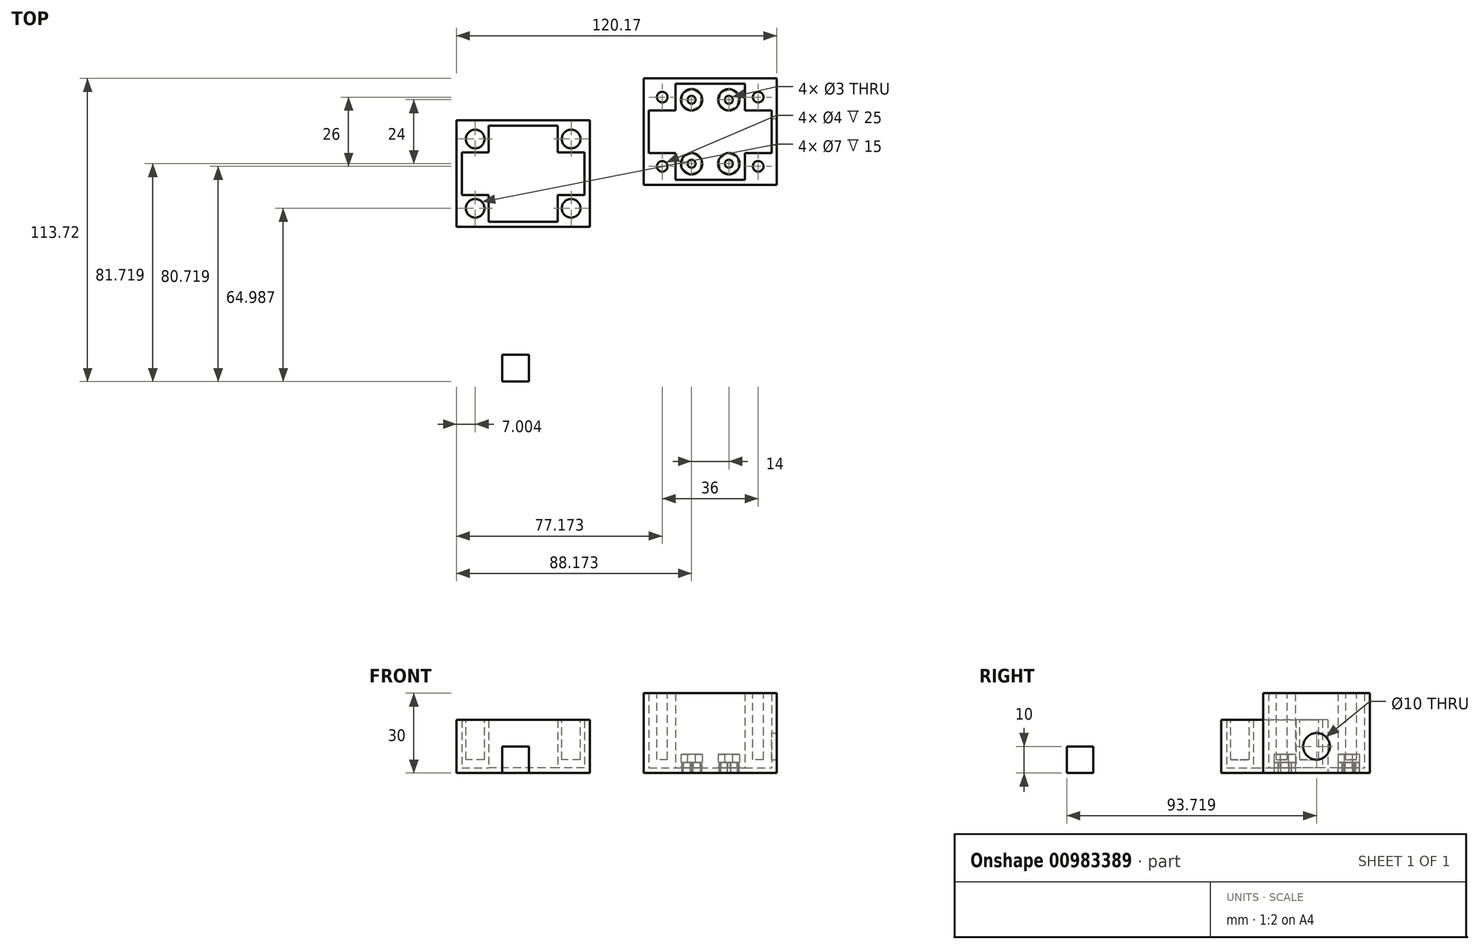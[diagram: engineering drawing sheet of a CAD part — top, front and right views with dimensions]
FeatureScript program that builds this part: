
annotation { "Feature Type Name" : "Feature", "Feature Type Description" : "" }
export const myFeature = defineFeature(function(context is Context, id is Id, definition is map)
    precondition{}
    {
        {
            var Q0;
            Q0=qCreatedBy(makeId("Top.planeOp"),FACE);
            var sketch = newSketch(context, id + "F0", { "sketchPlane" : qUnion([Q0])});
            skLineSegment(sketch, "E0.bottom", {"start": v(-58.4, 57.82) * mm, "end": v(-8.4, 57.82) * mm});
            skLineSegment(sketch, "E0.top", {"start": v(-58.4, 17.82) * mm, "end": v(-8.4, 17.82) * mm});
            skLineSegment(sketch, "E0.left", {"start": v(-58.4, 57.82) * mm, "end": v(-58.4, 17.82) * mm});
            skLineSegment(sketch, "E0.right", {"start": v(-8.4, 57.82) * mm, "end": v(-8.4, 17.82) * mm});
            skSolve(sketch);
        }
        {
            var Q0;
            Q0=makeQuery(id+"F0.imprint","IMPRINT",FACE,{"disambiguationData":[TD([[makeQuery(id+"F0.imprint","IMPRINT",EDGE,{"derivedFrom":sQuery(id+"F0.wireOp",EDGE,"E0.bottom")}),-1.0]])]});
            extrude(context, id + "F1", {"entities" : qUnion([Q0]), "depth" : 20 * mm, "offsetDistance" : 25 * mm});
        }
        {
            var Q0;
            Q0=makeQuery(id+"F1.opExtrude","CAP_FACE",FACE,{"disambiguationData":[OSD([sQuery(id+"F0.wireOp",EDGE,"E0.bottom"),sQuery(id+"F0.wireOp",EDGE,"E0.top"),sQuery(id+"F0.wireOp",EDGE,"E0.left"),sQuery(id+"F0.wireOp",EDGE,"E0.right")])],"isStart":false});
            var sketch = newSketch(context, id + "F2", { "sketchPlane" : qUnion([Q0])});
            skLineSegment(sketch, "E1.bottom", {"start": v(-10.4, 19.82) * mm, "end": v(-56.4, 19.82) * mm});
            skLineSegment(sketch, "E1.top", {"start": v(-10.4, 55.82) * mm, "end": v(-56.4, 55.82) * mm});
            skLineSegment(sketch, "E1.left", {"start": v(-10.4, 19.82) * mm, "end": v(-10.4, 55.82) * mm});
            skLineSegment(sketch, "E1.right", {"start": v(-56.4, 19.82) * mm, "end": v(-56.4, 55.82) * mm});
            skPoint(sketch, "E1.middle", {"position": v(-33.4, 37.82) * mm});
            skPoint(sketch, "E1.middle.positionSnap0", {"position": v(-58.4, 37.82) * mm});
            skPoint(sketch, "E1.middle.positionSnap1", {"position": v(-33.4, 57.82) * mm});
            skPoint(sketch, "E1.centerSnap0", {"position": v(-58.4, 37.82) * mm});
            skPoint(sketch, "E1.centerSnap1", {"position": v(-33.4, 57.82) * mm});
            skSolve(sketch);
        }
        {
            var Q0;
            Q0=makeQuery(id+"F2.imprint","IMPRINT",FACE,{"disambiguationData":[TD([[makeQuery(id+"F2.imprint","IMPRINT",EDGE,{"derivedFrom":sQuery(id+"F2.wireOp",EDGE,"E1.bottom")}),-1.0]])]});
            extrude(context, id + "F3", {"entities" : qUnion([Q0]), "operationType" : NewBodyOperationType.REMOVE, "oppositeDirection" : true, "depth" : 18 * mm, "offsetDistance" : 25 * mm});
        }
        {
            var Q0;
            Q0=makeQuery(id+"F3.boolean.opBoolean","COPY",FACE,{"derivedFrom":makeQuery(id+"F3.opExtrude","CAP_FACE",FACE,{"disambiguationData":[OSD([sQuery(id+"F2.wireOp",EDGE,"E1.bottom"),sQuery(id+"F2.wireOp",EDGE,"E1.top"),sQuery(id+"F2.wireOp",EDGE,"E1.left"),sQuery(id+"F2.wireOp",EDGE,"E1.right")])],"isStart":false})});
            var sketch = newSketch(context, id + "F4", { "sketchPlane" : qUnion([Q0])});
            skLineSegment(sketch, "E2.bottom", {"start": v(-56.4, 55.82) * mm, "end": v(-46.4, 55.82) * mm});
            skLineSegment(sketch, "E2.top", {"start": v(-56.4, 45.82) * mm, "end": v(-46.4, 45.82) * mm});
            skLineSegment(sketch, "E2.left", {"start": v(-56.4, 55.82) * mm, "end": v(-56.4, 45.82) * mm});
            skLineSegment(sketch, "E2.right", {"start": v(-46.4, 55.82) * mm, "end": v(-46.4, 45.82) * mm});
            skLineSegment(sketch, "E3.bottom", {"start": v(-10.4, 55.82) * mm, "end": v(-20.4, 55.82) * mm});
            skLineSegment(sketch, "E3.top", {"start": v(-10.4, 45.82) * mm, "end": v(-20.4, 45.82) * mm});
            skLineSegment(sketch, "E3.left", {"start": v(-10.4, 55.82) * mm, "end": v(-10.4, 45.82) * mm});
            skLineSegment(sketch, "E3.right", {"start": v(-20.4, 55.82) * mm, "end": v(-20.4, 45.82) * mm});
            skLineSegment(sketch, "E4.bottom", {"start": v(-10.4, 19.82) * mm, "end": v(-20.4, 19.82) * mm});
            skLineSegment(sketch, "E4.top", {"start": v(-10.4, 29.82) * mm, "end": v(-20.4, 29.82) * mm});
            skLineSegment(sketch, "E4.left", {"start": v(-10.4, 19.82) * mm, "end": v(-10.4, 29.82) * mm});
            skLineSegment(sketch, "E4.right", {"start": v(-20.4, 19.82) * mm, "end": v(-20.4, 29.82) * mm});
            skLineSegment(sketch, "E5.bottom", {"start": v(-56.4, 19.82) * mm, "end": v(-46.4, 19.82) * mm});
            skLineSegment(sketch, "E5.top", {"start": v(-56.4, 29.82) * mm, "end": v(-46.4, 29.82) * mm});
            skLineSegment(sketch, "E5.left", {"start": v(-56.4, 19.82) * mm, "end": v(-56.4, 29.82) * mm});
            skLineSegment(sketch, "E5.right", {"start": v(-46.4, 19.82) * mm, "end": v(-46.4, 29.82) * mm});
            skSolve(sketch);
        }
        {
            var Q0;
            Q0=makeQuery(id+"F4.imprint","IMPRINT",FACE,{"disambiguationData":[TD([[makeQuery(id+"F4.imprint","IMPRINT",EDGE,{"derivedFrom":sQuery(id+"F4.wireOp",EDGE,"E2.bottom")}),1.0]])]});
            var Q1;
            Q1=makeQuery(id+"F4.imprint","IMPRINT",FACE,{"disambiguationData":[TD([[makeQuery(id+"F4.imprint","IMPRINT",EDGE,{"derivedFrom":sQuery(id+"F4.wireOp",EDGE,"E3.bottom")}),1.0]])]});
            var Q2;
            Q2=makeQuery(id+"F4.imprint","IMPRINT",FACE,{"disambiguationData":[TD([[makeQuery(id+"F4.imprint","IMPRINT",EDGE,{"derivedFrom":sQuery(id+"F4.wireOp",EDGE,"E4.bottom")}),-1.0]])]});
            var Q3;
            Q3=makeQuery(id+"F4.imprint","IMPRINT",FACE,{"disambiguationData":[TD([[makeQuery(id+"F4.imprint","IMPRINT",EDGE,{"derivedFrom":sQuery(id+"F4.wireOp",EDGE,"E5.bottom")}),-1.0]])]});
            extrude(context, id + "F5", {"entities" : qUnion([Q0, Q1, Q2, Q3]), "operationType" : NewBodyOperationType.ADD, "depth" : 18 * mm, "offsetDistance" : 25 * mm});
        }
        {
            var Q0;
            Q0=makeQuery(id+"F5.boolean.opBoolean","MERGE",FACE,{"derivedFrom":[makeQuery(id+"F1.opExtrude","CAP_FACE",FACE,{"disambiguationData":[OSD([sQuery(id+"F0.wireOp",EDGE,"E0.bottom"),sQuery(id+"F0.wireOp",EDGE,"E0.top"),sQuery(id+"F0.wireOp",EDGE,"E0.left"),sQuery(id+"F0.wireOp",EDGE,"E0.right")])],"isStart":false}),makeQuery(id+"F5.opExtrude","CAP_FACE",FACE,{"disambiguationData":[OSD([sQuery(id+"F4.wireOp",EDGE,"E2.bottom"),sQuery(id+"F4.wireOp",EDGE,"E2.top"),sQuery(id+"F4.wireOp",EDGE,"E2.left"),sQuery(id+"F4.wireOp",EDGE,"E2.right")])],"isStart":false}),makeQuery(id+"F5.opExtrude","CAP_FACE",FACE,{"disambiguationData":[OSD([sQuery(id+"F4.wireOp",EDGE,"E3.bottom"),sQuery(id+"F4.wireOp",EDGE,"E3.top"),sQuery(id+"F4.wireOp",EDGE,"E3.left"),sQuery(id+"F4.wireOp",EDGE,"E3.right")])],"isStart":false}),makeQuery(id+"F5.opExtrude","CAP_FACE",FACE,{"disambiguationData":[OSD([sQuery(id+"F4.wireOp",EDGE,"E4.bottom"),sQuery(id+"F4.wireOp",EDGE,"E4.top"),sQuery(id+"F4.wireOp",EDGE,"E4.left"),sQuery(id+"F4.wireOp",EDGE,"E4.right")])],"isStart":false}),makeQuery(id+"F5.opExtrude","CAP_FACE",FACE,{"disambiguationData":[OSD([sQuery(id+"F4.wireOp",EDGE,"E5.bottom"),sQuery(id+"F4.wireOp",EDGE,"E5.top"),sQuery(id+"F4.wireOp",EDGE,"E5.left"),sQuery(id+"F4.wireOp",EDGE,"E5.right")])],"isStart":false})]});
            var sketch = newSketch(context, id + "F6", { "sketchPlane" : qUnion([Q0])});
            skCircle(sketch, "E6", {"center": v(-51.4, 50.82) * mm, "radius": 3.5 * mm});
            skPoint(sketch, "E6.centerSnap0", {"position": v(-51.4, 45.82) * mm});
            skPoint(sketch, "E6.centerSnap1", {"position": v(-46.4, 50.82) * mm});
            skCircle(sketch, "E7", {"center": v(-15.4, 50.82) * mm, "radius": 3.5 * mm});
            skPoint(sketch, "E7.centerSnap0", {"position": v(-20.4, 50.82) * mm});
            skPoint(sketch, "E7.centerSnap1", {"position": v(-15.4, 45.82) * mm});
            skCircle(sketch, "E8", {"center": v(-15.4, 24.82) * mm, "radius": 3.5 * mm});
            skPoint(sketch, "E8.centerSnap0", {"position": v(-20.4, 24.82) * mm});
            skPoint(sketch, "E8.centerSnap1", {"position": v(-15.4, 29.82) * mm});
            skCircle(sketch, "E9", {"center": v(-51.4, 24.82) * mm, "radius": 3.5 * mm});
            skPoint(sketch, "E9.centerSnap0", {"position": v(-51.4, 29.82) * mm});
            skPoint(sketch, "E9.centerSnap1", {"position": v(-46.4, 24.82) * mm});
            skSolve(sketch);
        }
        {
            var Q0;
            Q0=makeQuery(id+"F6.imprint","IMPRINT",FACE,{"disambiguationData":[TD([[makeQuery(id+"F6.imprint","IMPRINT",EDGE,{"derivedFrom":sQuery(id+"F6.wireOp",EDGE,"E6")}),1.0]])]});
            var Q1;
            Q1=makeQuery(id+"F6.imprint","IMPRINT",FACE,{"disambiguationData":[TD([[makeQuery(id+"F6.imprint","IMPRINT",EDGE,{"derivedFrom":sQuery(id+"F6.wireOp",EDGE,"E7")}),1.0]])]});
            var Q2;
            Q2=makeQuery(id+"F6.imprint","IMPRINT",FACE,{"disambiguationData":[TD([[makeQuery(id+"F6.imprint","IMPRINT",EDGE,{"derivedFrom":sQuery(id+"F6.wireOp",EDGE,"E8")}),1.0]])]});
            var Q3;
            Q3=makeQuery(id+"F6.imprint","IMPRINT",FACE,{"disambiguationData":[TD([[makeQuery(id+"F6.imprint","IMPRINT",EDGE,{"derivedFrom":sQuery(id+"F6.wireOp",EDGE,"E9")}),1.0]])]});
            extrude(context, id + "F7", {"entities" : qUnion([Q0, Q1, Q2, Q3]), "operationType" : NewBodyOperationType.REMOVE, "oppositeDirection" : true, "depth" : 15 * mm, "offsetDistance" : 25 * mm});
        }
        {
            var Q0;
            Q0=qCreatedBy(makeId("Top.planeOp"),FACE);
            var sketch = newSketch(context, id + "F8", { "sketchPlane" : qUnion([Q0])});
            skLineSegment(sketch, "E10.bottom", {"start": v(-41.2, -30.17) * mm, "end": v(-31.2, -30.17) * mm});
            skLineSegment(sketch, "E10.top", {"start": v(-41.2, -40.17) * mm, "end": v(-31.2, -40.17) * mm});
            skLineSegment(sketch, "E10.left", {"start": v(-41.2, -30.17) * mm, "end": v(-41.2, -40.17) * mm});
            skLineSegment(sketch, "E10.right", {"start": v(-31.2, -30.17) * mm, "end": v(-31.2, -40.17) * mm});
            skSolve(sketch);
        }
        {
            var Q0;
            Q0=makeQuery(id+"F8.imprint","IMPRINT",FACE,{"disambiguationData":[TD([[makeQuery(id+"F8.imprint","IMPRINT",EDGE,{"derivedFrom":sQuery(id+"F8.wireOp",EDGE,"E10.bottom")}),-1.0]])]});
            extrude(context, id + "F9", {"entities" : qUnion([Q0]), "depth" : 10 * mm, "offsetDistance" : 25 * mm});
        }
        {
            var Q0;
            Q0=qCreatedBy(makeId("Top.planeOp"),FACE);
            var sketch = newSketch(context, id + "F10", { "sketchPlane" : qUnion([Q0])});
            skLineSegment(sketch, "E11.bottom", {"start": v(11.76, 73.55) * mm, "end": v(61.76, 73.55) * mm});
            skLineSegment(sketch, "E11.top", {"start": v(11.76, 33.55) * mm, "end": v(61.76, 33.55) * mm});
            skLineSegment(sketch, "E11.left", {"start": v(11.76, 73.55) * mm, "end": v(11.76, 33.55) * mm});
            skLineSegment(sketch, "E11.right", {"start": v(61.76, 73.55) * mm, "end": v(61.76, 33.55) * mm});
            skSolve(sketch);
        }
        {
            var Q0;
            Q0 = qSketchRegion(id + "F10", true);
            extrude(context, id + "F11", {"entities" : qUnion([Q0]), "operationType" : NewBodyOperationType.ADD, "depth" : 30 * mm, "offsetDistance" : 25 * mm});
        }
        {
            var Q0;
            Q0=makeQuery(id+"F11.opExtrude","CAP_FACE",FACE,{"disambiguationData":[OSD([sQuery(id+"F10.wireOp",EDGE,"E11.bottom"),sQuery(id+"F10.wireOp",EDGE,"E11.top"),sQuery(id+"F10.wireOp",EDGE,"E11.left"),sQuery(id+"F10.wireOp",EDGE,"E11.right")])],"isStart":false});
            var sketch = newSketch(context, id + "F12", { "sketchPlane" : qUnion([Q0])});
            skLineSegment(sketch, "E12.bottom", {"start": v(13.76, 71.55) * mm, "end": v(59.76, 71.55) * mm});
            skLineSegment(sketch, "E12.top", {"start": v(13.76, 35.55) * mm, "end": v(59.76, 35.55) * mm});
            skLineSegment(sketch, "E12.left", {"start": v(13.76, 71.55) * mm, "end": v(13.76, 35.55) * mm});
            skLineSegment(sketch, "E12.right", {"start": v(59.76, 71.55) * mm, "end": v(59.76, 35.55) * mm});
            skSolve(sketch);
        }
        {
            var Q0;
            Q0=makeQuery(id+"F12.imprint","IMPRINT",FACE,{"disambiguationData":[TD([[makeQuery(id+"F12.imprint","IMPRINT",EDGE,{"derivedFrom":sQuery(id+"F12.wireOp",EDGE,"E12.bottom")}),-1.0]])]});
            extrude(context, id + "F13", {"entities" : qUnion([Q0]), "operationType" : NewBodyOperationType.REMOVE, "oppositeDirection" : true, "depth" : 28 * mm, "offsetDistance" : 25 * mm});
        }
        {
            var Q0;
            Q0=makeQuery(id+"F13.boolean.opBoolean","COPY",FACE,{"derivedFrom":makeQuery(id+"F13.opExtrude","CAP_FACE",FACE,{"disambiguationData":[OSD([sQuery(id+"F12.wireOp",EDGE,"E12.bottom"),sQuery(id+"F12.wireOp",EDGE,"E12.top"),sQuery(id+"F12.wireOp",EDGE,"E12.left"),sQuery(id+"F12.wireOp",EDGE,"E12.right")])],"isStart":false})});
            var sketch = newSketch(context, id + "F14", { "sketchPlane" : qUnion([Q0])});
            skLineSegment(sketch, "E13.bottom", {"start": v(13.76, 71.55) * mm, "end": v(23.76, 71.55) * mm});
            skLineSegment(sketch, "E13.top", {"start": v(13.76, 61.55) * mm, "end": v(23.76, 61.55) * mm});
            skLineSegment(sketch, "E13.left", {"start": v(13.76, 71.55) * mm, "end": v(13.76, 61.55) * mm});
            skLineSegment(sketch, "E13.right", {"start": v(23.76, 71.55) * mm, "end": v(23.76, 61.55) * mm});
            skLineSegment(sketch, "E14.bottom", {"start": v(49.76, 61.55) * mm, "end": v(59.76, 61.55) * mm});
            skLineSegment(sketch, "E14.top", {"start": v(49.76, 71.55) * mm, "end": v(59.76, 71.55) * mm});
            skLineSegment(sketch, "E14.left", {"start": v(49.76, 61.55) * mm, "end": v(49.76, 71.55) * mm});
            skLineSegment(sketch, "E14.right", {"start": v(59.76, 61.55) * mm, "end": v(59.76, 71.55) * mm});
            skLineSegment(sketch, "E15.bottom", {"start": v(23.76, 45.55) * mm, "end": v(13.76, 45.55) * mm});
            skLineSegment(sketch, "E15.top", {"start": v(23.76, 35.55) * mm, "end": v(13.76, 35.55) * mm});
            skLineSegment(sketch, "E15.left", {"start": v(23.76, 45.55) * mm, "end": v(23.76, 35.55) * mm});
            skLineSegment(sketch, "E15.right", {"start": v(13.76, 45.55) * mm, "end": v(13.76, 35.55) * mm});
            skLineSegment(sketch, "E16.bottom", {"start": v(49.76, 45.55) * mm, "end": v(59.76, 45.55) * mm});
            skLineSegment(sketch, "E16.top", {"start": v(49.76, 35.55) * mm, "end": v(59.76, 35.55) * mm});
            skLineSegment(sketch, "E16.left", {"start": v(49.76, 45.55) * mm, "end": v(49.76, 35.55) * mm});
            skLineSegment(sketch, "E16.right", {"start": v(59.76, 45.55) * mm, "end": v(59.76, 35.55) * mm});
            skSolve(sketch);
        }
        {
            var Q0;
            Q0=makeQuery(id+"F14.imprint","IMPRINT",FACE,{"disambiguationData":[TD([[makeQuery(id+"F14.imprint","IMPRINT",EDGE,{"derivedFrom":sQuery(id+"F14.wireOp",EDGE,"E13.bottom")}),-1.0]])]});
            var Q1;
            Q1=makeQuery(id+"F14.imprint","IMPRINT",FACE,{"disambiguationData":[TD([[makeQuery(id+"F14.imprint","IMPRINT",EDGE,{"derivedFrom":sQuery(id+"F14.wireOp",EDGE,"E15.bottom")}),1.0]])]});
            var Q2;
            Q2=makeQuery(id+"F14.imprint","IMPRINT",FACE,{"disambiguationData":[TD([[makeQuery(id+"F14.imprint","IMPRINT",EDGE,{"derivedFrom":sQuery(id+"F14.wireOp",EDGE,"E14.bottom")}),1.0]])]});
            var Q3;
            Q3=makeQuery(id+"F14.imprint","IMPRINT",FACE,{"disambiguationData":[TD([[makeQuery(id+"F14.imprint","IMPRINT",EDGE,{"derivedFrom":sQuery(id+"F14.wireOp",EDGE,"E16.bottom")}),-1.0]])]});
            extrude(context, id + "F15", {"entities" : qUnion([Q0, Q1, Q2, Q3]), "operationType" : NewBodyOperationType.ADD, "depth" : 28 * mm, "offsetDistance" : 25 * mm});
        }
        {
            var Q0;
            Q0=makeQuery(id+"F15.boolean.opBoolean","MERGE",FACE,{"derivedFrom":[makeQuery(id+"F11.opExtrude","CAP_FACE",FACE,{"disambiguationData":[OSD([sQuery(id+"F10.wireOp",EDGE,"E11.bottom"),sQuery(id+"F10.wireOp",EDGE,"E11.top"),sQuery(id+"F10.wireOp",EDGE,"E11.left"),sQuery(id+"F10.wireOp",EDGE,"E11.right")])],"isStart":false}),makeQuery(id+"F15.opExtrude","CAP_FACE",FACE,{"disambiguationData":[OSD([sQuery(id+"F14.wireOp",EDGE,"E13.bottom"),sQuery(id+"F14.wireOp",EDGE,"E13.top"),sQuery(id+"F14.wireOp",EDGE,"E13.left"),sQuery(id+"F14.wireOp",EDGE,"E13.right")])],"isStart":false}),makeQuery(id+"F15.opExtrude","CAP_FACE",FACE,{"disambiguationData":[OSD([sQuery(id+"F14.wireOp",EDGE,"E14.bottom"),sQuery(id+"F14.wireOp",EDGE,"E14.top"),sQuery(id+"F14.wireOp",EDGE,"E14.left"),sQuery(id+"F14.wireOp",EDGE,"E14.right")])],"isStart":false}),makeQuery(id+"F15.opExtrude","CAP_FACE",FACE,{"disambiguationData":[OSD([sQuery(id+"F14.wireOp",EDGE,"E15.bottom"),sQuery(id+"F14.wireOp",EDGE,"E15.top"),sQuery(id+"F14.wireOp",EDGE,"E15.left"),sQuery(id+"F14.wireOp",EDGE,"E15.right")])],"isStart":false}),makeQuery(id+"F15.opExtrude","CAP_FACE",FACE,{"disambiguationData":[OSD([sQuery(id+"F14.wireOp",EDGE,"E16.bottom"),sQuery(id+"F14.wireOp",EDGE,"E16.top"),sQuery(id+"F14.wireOp",EDGE,"E16.left"),sQuery(id+"F14.wireOp",EDGE,"E16.right")])],"isStart":false})]});
            var sketch = newSketch(context, id + "F16", { "sketchPlane" : qUnion([Q0])});
            skCircle(sketch, "E17", {"center": v(18.76, 66.55) * mm, "radius": 2 * mm});
            skPoint(sketch, "E17.centerSnap0", {"position": v(23.76, 66.55) * mm});
            skPoint(sketch, "E17.centerSnap1", {"position": v(18.76, 61.55) * mm});
            skCircle(sketch, "E18", {"center": v(54.76, 66.55) * mm, "radius": 2 * mm});
            skPoint(sketch, "E18.centerSnap0", {"position": v(54.76, 61.55) * mm});
            skPoint(sketch, "E18.centerSnap1", {"position": v(49.76, 66.55) * mm});
            skCircle(sketch, "E19", {"center": v(18.76, 40.55) * mm, "radius": 2 * mm});
            skPoint(sketch, "E19.centerSnap0", {"position": v(18.76, 45.55) * mm});
            skPoint(sketch, "E19.centerSnap1", {"position": v(23.76, 40.55) * mm});
            skCircle(sketch, "E20", {"center": v(54.76, 40.55) * mm, "radius": 2 * mm});
            skPoint(sketch, "E20.centerSnap0", {"position": v(54.76, 45.55) * mm});
            skPoint(sketch, "E20.centerSnap1", {"position": v(49.76, 40.55) * mm});
            skSolve(sketch);
        }
        {
            var Q0;
            Q0=makeQuery(id+"F16.imprint","IMPRINT",FACE,{"disambiguationData":[TD([[makeQuery(id+"F16.imprint","IMPRINT",EDGE,{"derivedFrom":sQuery(id+"F16.wireOp",EDGE,"E17")}),1.0]])]});
            var Q1;
            Q1=makeQuery(id+"F16.imprint","IMPRINT",FACE,{"disambiguationData":[TD([[makeQuery(id+"F16.imprint","IMPRINT",EDGE,{"derivedFrom":sQuery(id+"F16.wireOp",EDGE,"E18")}),1.0]])]});
            var Q2;
            Q2=makeQuery(id+"F16.imprint","IMPRINT",FACE,{"disambiguationData":[TD([[makeQuery(id+"F16.imprint","IMPRINT",EDGE,{"derivedFrom":sQuery(id+"F16.wireOp",EDGE,"E20")}),1.0]])]});
            var Q3;
            Q3=makeQuery(id+"F16.imprint","IMPRINT",FACE,{"disambiguationData":[TD([[makeQuery(id+"F16.imprint","IMPRINT",EDGE,{"derivedFrom":sQuery(id+"F16.wireOp",EDGE,"E19")}),1.0]])]});
            extrude(context, id + "F17", {"entities" : qUnion([Q0, Q1, Q2, Q3]), "operationType" : NewBodyOperationType.REMOVE, "oppositeDirection" : true, "depth" : 25 * mm, "offsetDistance" : 25 * mm});
        }
        {
            var Q0;
            Q0=makeQuery(id+"F13.boolean.opBoolean","COPY",FACE,{"derivedFrom":makeQuery(id+"F13.opExtrude","CAP_FACE",FACE,{"disambiguationData":[OSD([sQuery(id+"F12.wireOp",EDGE,"E12.bottom"),sQuery(id+"F12.wireOp",EDGE,"E12.top"),sQuery(id+"F12.wireOp",EDGE,"E12.left"),sQuery(id+"F12.wireOp",EDGE,"E12.right")])],"isStart":false})});
            var sketch = newSketch(context, id + "F18", { "sketchPlane" : qUnion([Q0])});
            skCircle(sketch, "E21", {"center": v(29.76, 65.55) * mm, "radius": 4 * mm});
            skCircle(sketch, "E22", {"center": v(43.76, 65.55) * mm, "radius": 4 * mm});
            skCircle(sketch, "E23", {"center": v(29.76, 41.55) * mm, "radius": 4 * mm});
            skCircle(sketch, "E24", {"center": v(43.76, 41.55) * mm, "radius": 4 * mm});
            skSolve(sketch);
        }
        {
            var Q0;
            Q0=makeQuery(id+"F18.imprint","IMPRINT",FACE,{"disambiguationData":[TD([[makeQuery(id+"F18.imprint","IMPRINT",EDGE,{"derivedFrom":sQuery(id+"F18.wireOp",EDGE,"E21")}),1.0]])]});
            var Q1;
            Q1=makeQuery(id+"F18.imprint","IMPRINT",FACE,{"disambiguationData":[TD([[makeQuery(id+"F18.imprint","IMPRINT",EDGE,{"derivedFrom":sQuery(id+"F18.wireOp",EDGE,"E22")}),1.0]])]});
            var Q2;
            Q2=makeQuery(id+"F18.imprint","IMPRINT",FACE,{"disambiguationData":[TD([[makeQuery(id+"F18.imprint","IMPRINT",EDGE,{"derivedFrom":sQuery(id+"F18.wireOp",EDGE,"E23")}),1.0]])]});
            var Q3;
            Q3=makeQuery(id+"F18.imprint","IMPRINT",FACE,{"disambiguationData":[TD([[makeQuery(id+"F18.imprint","IMPRINT",EDGE,{"derivedFrom":sQuery(id+"F18.wireOp",EDGE,"E24")}),1.0]])]});
            extrude(context, id + "F19", {"entities" : qUnion([Q0, Q1, Q2, Q3]), "operationType" : NewBodyOperationType.ADD, "depth" : 5 * mm, "offsetDistance" : 25 * mm});
        }
        {
            var Q0;
            Q0=makeQuery(id+"F19.opExtrude","CAP_FACE",FACE,{"disambiguationData":[OSD([sQuery(id+"F18.wireOp",EDGE,"E23")])],"isStart":false});
            var sketch = newSketch(context, id + "F20", { "sketchPlane" : qUnion([Q0])});
            skCircle(sketch, "E25", {"center": v(29.76, 41.55) * mm, "radius": 1.5 * mm});
            skSolve(sketch);
        }
        {
            var Q0;
            Q0=makeQuery(id+"F19.opExtrude","CAP_FACE",FACE,{"disambiguationData":[OSD([sQuery(id+"F18.wireOp",EDGE,"E24")])],"isStart":false});
            var sketch = newSketch(context, id + "F21", { "sketchPlane" : qUnion([Q0])});
            skCircle(sketch, "E26", {"center": v(43.76, 41.55) * mm, "radius": 1.5 * mm});
            skSolve(sketch);
        }
        {
            var Q0;
            Q0=makeQuery(id+"F19.opExtrude","CAP_FACE",FACE,{"disambiguationData":[OSD([sQuery(id+"F18.wireOp",EDGE,"E21")])],"isStart":false});
            var sketch = newSketch(context, id + "F22", { "sketchPlane" : qUnion([Q0])});
            skCircle(sketch, "E27", {"center": v(29.76, 65.55) * mm, "radius": 1.5 * mm});
            skSolve(sketch);
        }
        {
            var Q0;
            Q0=makeQuery(id+"F19.opExtrude","CAP_FACE",FACE,{"disambiguationData":[OSD([sQuery(id+"F18.wireOp",EDGE,"E22")])],"isStart":false});
            var sketch = newSketch(context, id + "F23", { "sketchPlane" : qUnion([Q0])});
            skCircle(sketch, "E28", {"center": v(43.76, 65.55) * mm, "radius": 1.5 * mm});
            skSolve(sketch);
        }
        {
            var Q0;
            Q0=makeQuery(id+"F22.imprint","IMPRINT",FACE,{"disambiguationData":[TD([[makeQuery(id+"F22.imprint","IMPRINT",EDGE,{"derivedFrom":sQuery(id+"F22.wireOp",EDGE,"E27")}),1.0]])]});
            var Q1;
            Q1=makeQuery(id+"F23.imprint","IMPRINT",FACE,{"disambiguationData":[TD([[makeQuery(id+"F23.imprint","IMPRINT",EDGE,{"derivedFrom":sQuery(id+"F23.wireOp",EDGE,"E28")}),1.0]])]});
            var Q2;
            Q2=makeQuery(id+"F21.imprint","IMPRINT",FACE,{"disambiguationData":[TD([[makeQuery(id+"F21.imprint","IMPRINT",EDGE,{"derivedFrom":sQuery(id+"F21.wireOp",EDGE,"E26")}),1.0]])]});
            var Q3;
            Q3=makeQuery(id+"F20.imprint","IMPRINT",FACE,{"disambiguationData":[TD([[makeQuery(id+"F20.imprint","IMPRINT",EDGE,{"derivedFrom":sQuery(id+"F20.wireOp",EDGE,"E25")}),1.0]])]});
            extrude(context, id + "F24", {"entities" : qUnion([Q0, Q1, Q2, Q3]), "operationType" : NewBodyOperationType.REMOVE, "oppositeDirection" : true, "depth" : 10 * mm, "offsetDistance" : 25 * mm});
        }
        {
            var Q0;
            Q0=makeQuery(id+"F11.opExtrude","CAP_FACE",FACE,{"disambiguationData":[OSD([sQuery(id+"F10.wireOp",EDGE,"E11.bottom"),sQuery(id+"F10.wireOp",EDGE,"E11.top"),sQuery(id+"F10.wireOp",EDGE,"E11.left"),sQuery(id+"F10.wireOp",EDGE,"E11.right")])],"isStart":true});
            var sketch = newSketch(context, id + "F25", { "sketchPlane" : qUnion([Q0])});
            skCircle(sketch, "E29.cCircle", {"center": v(29.76, -41.55) * mm, "radius": 3.5 * mm, "construction": true});
            skLineSegment(sketch, "E29.0", {"start": v(33, -39.12) * mm, "end": v(33.48, -43.13) * mm});
            skLineSegment(sketch, "E29.1", {"start": v(33.48, -43.13) * mm, "end": v(30.25, -45.56) * mm});
            skLineSegment(sketch, "E29.2", {"start": v(30.25, -45.56) * mm, "end": v(26.53, -43.98) * mm});
            skLineSegment(sketch, "E29.3", {"start": v(26.53, -43.98) * mm, "end": v(26.04, -39.97) * mm});
            skLineSegment(sketch, "E29.4", {"start": v(26.04, -39.97) * mm, "end": v(29.27, -37.54) * mm});
            skLineSegment(sketch, "E29.5", {"start": v(29.27, -37.54) * mm, "end": v(33, -39.12) * mm});
            skPoint(sketch, "E29.0.midPoint", {"position": v(33.24, -41.12) * mm});
            skCircle(sketch, "E30.cCircle", {"center": v(43.76, -41.55) * mm, "radius": 3.5 * mm, "construction": true});
            skLineSegment(sketch, "E30.0", {"start": v(40.02, -43.08) * mm, "end": v(40.57, -39.08) * mm});
            skLineSegment(sketch, "E30.1", {"start": v(40.57, -39.08) * mm, "end": v(44.3, -37.54) * mm});
            skLineSegment(sketch, "E30.2", {"start": v(44.3, -37.54) * mm, "end": v(47.5, -40.02) * mm});
            skLineSegment(sketch, "E30.3", {"start": v(47.5, -40.02) * mm, "end": v(46.96, -44.02) * mm});
            skLineSegment(sketch, "E30.4", {"start": v(46.96, -44.02) * mm, "end": v(43.22, -45.55) * mm});
            skLineSegment(sketch, "E30.5", {"start": v(43.22, -45.55) * mm, "end": v(40.02, -43.08) * mm});
            skPoint(sketch, "E30.0.midPoint", {"position": v(40.3, -41.08) * mm});
            skCircle(sketch, "E31.cCircle", {"center": v(29.76, -65.55) * mm, "radius": 3.5 * mm, "construction": true});
            skLineSegment(sketch, "E31.0", {"start": v(26.16, -63.71) * mm, "end": v(29.55, -61.51) * mm});
            skLineSegment(sketch, "E31.1", {"start": v(29.55, -61.51) * mm, "end": v(33.15, -63.35) * mm});
            skLineSegment(sketch, "E31.2", {"start": v(33.15, -63.35) * mm, "end": v(33.36, -67.38) * mm});
            skLineSegment(sketch, "E31.3", {"start": v(33.36, -67.38) * mm, "end": v(29.98, -69.58) * mm});
            skLineSegment(sketch, "E31.4", {"start": v(29.98, -69.58) * mm, "end": v(26.37, -67.75) * mm});
            skLineSegment(sketch, "E31.5", {"start": v(26.37, -67.75) * mm, "end": v(26.16, -63.71) * mm});
            skPoint(sketch, "E31.0.midPoint", {"position": v(27.86, -62.61) * mm});
            skCircle(sketch, "E32.cCircle", {"center": v(43.76, -65.55) * mm, "radius": 3.5 * mm, "construction": true});
            skLineSegment(sketch, "E32.0", {"start": v(39.97, -64.15) * mm, "end": v(43.08, -61.57) * mm});
            skLineSegment(sketch, "E32.1", {"start": v(43.08, -61.57) * mm, "end": v(46.87, -62.97) * mm});
            skLineSegment(sketch, "E32.2", {"start": v(46.87, -62.97) * mm, "end": v(47.55, -66.95) * mm});
            skLineSegment(sketch, "E32.3", {"start": v(47.55, -66.95) * mm, "end": v(44.44, -69.53) * mm});
            skLineSegment(sketch, "E32.4", {"start": v(44.44, -69.53) * mm, "end": v(40.65, -68.13) * mm});
            skLineSegment(sketch, "E32.5", {"start": v(40.65, -68.13) * mm, "end": v(39.97, -64.15) * mm});
            skPoint(sketch, "E32.0.midPoint", {"position": v(41.53, -62.86) * mm});
            skSolve(sketch);
        }
        {
            var Q0;
            Q0=makeQuery(id+"F25.imprint","IMPRINT",FACE,{"disambiguationData":[TD([[makeQuery(id+"F25.imprint","IMPRINT",EDGE,{"derivedFrom":sQuery(id+"F25.wireOp",EDGE,"E29.0")}),-1.0]])]});
            var Q1;
            Q1=makeQuery(id+"F25.imprint","IMPRINT",FACE,{"disambiguationData":[TD([[makeQuery(id+"F25.imprint","IMPRINT",EDGE,{"derivedFrom":sQuery(id+"F25.wireOp",EDGE,"E30.0")}),-1.0]])]});
            var Q2;
            Q2=makeQuery(id+"F25.imprint","IMPRINT",FACE,{"disambiguationData":[TD([[makeQuery(id+"F25.imprint","IMPRINT",EDGE,{"derivedFrom":sQuery(id+"F25.wireOp",EDGE,"E32.0")}),-1.0]])]});
            var Q3;
            Q3=makeQuery(id+"F25.imprint","IMPRINT",FACE,{"disambiguationData":[TD([[makeQuery(id+"F25.imprint","IMPRINT",EDGE,{"derivedFrom":sQuery(id+"F25.wireOp",EDGE,"E31.0")}),-1.0]])]});
            extrude(context, id + "F26", {"entities" : qUnion([Q0, Q1, Q2, Q3]), "operationType" : NewBodyOperationType.REMOVE, "oppositeDirection" : true, "depth" : 4 * mm, "offsetDistance" : 25 * mm});
        }
        {
            var Q0;
            Q0=makeQuery(id+"F11.opExtrude","SWEPT_FACE",FACE,{"disambiguationData":[OSD([sQuery(id+"F10.wireOp",EDGE,"E11.right")])]});
            var sketch = newSketch(context, id + "F27", { "sketchPlane" : qUnion([Q0])});
            skCircle(sketch, "E33", {"center": v(53.55, 10) * mm, "radius": 5 * mm});
            skPoint(sketch, "E33.centerSnap0", {"position": v(53.55, 30) * mm});
            skSolve(sketch);
        }
        {
            var Q0;
            Q0=makeQuery(id+"F27.imprint","IMPRINT",FACE,{"disambiguationData":[TD([[makeQuery(id+"F27.imprint","IMPRINT",EDGE,{"derivedFrom":sQuery(id+"F27.wireOp",EDGE,"E33")}),1.0]])]});
            extrude(context, id + "F28", {"entities" : qUnion([Q0]), "operationType" : NewBodyOperationType.REMOVE, "oppositeDirection" : true, "depth" : 2 * mm, "offsetDistance" : 25 * mm});
        }
    });
